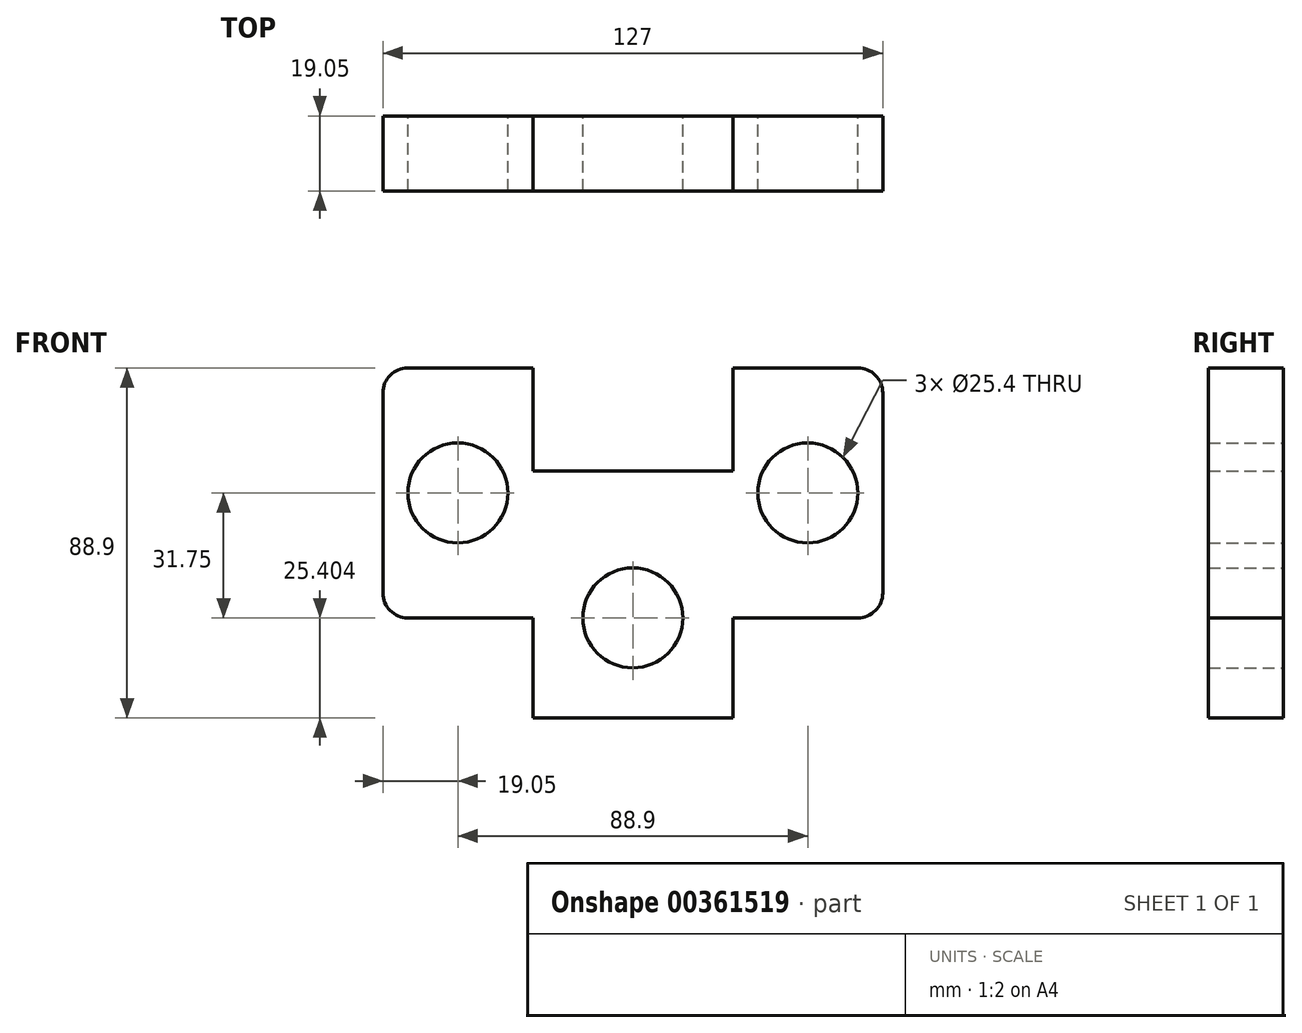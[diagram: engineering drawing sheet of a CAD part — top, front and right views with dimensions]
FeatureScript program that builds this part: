
annotation { "Feature Type Name" : "Feature", "Feature Type Description" : "" }
export const myFeature = defineFeature(function(context is Context, id is Id, definition is map)
    precondition{}
    {
        {
            var Q0;
            Q0=qCreatedBy(makeId("Front.planeOp"),FACE);
            var sketch = newSketch(context, id + "F0", { "sketchPlane" : qUnion([Q0])});
            skLineSegment(sketch, "E0", {"start": v(-74.8, 46.27) * mm, "end": v(-43.06, 46.27) * mm});
            skLineSegment(sketch, "E1", {"start": v(-43.06, 46.27) * mm, "end": v(-43.06, 20.11) * mm});
            skLineSegment(sketch, "E2", {"start": v(-43.06, 20.11) * mm, "end": v(7.74, 20.11) * mm});
            skLineSegment(sketch, "E3", {"start": v(7.74, 20.11) * mm, "end": v(7.74, 46.27) * mm});
            skLineSegment(sketch, "E4", {"start": v(7.74, 46.27) * mm, "end": v(39.5, 46.27) * mm});
            skLineSegment(sketch, "E5", {"start": v(45.84, 39.92) * mm, "end": v(45.84, -10.88) * mm});
            skLineSegment(sketch, "E6", {"start": v(39.5, -17.23) * mm, "end": v(7.74, -17.23) * mm});
            skLineSegment(sketch, "E7", {"start": v(7.74, -17.23) * mm, "end": v(7.74, -42.63) * mm});
            skLineSegment(sketch, "E8", {"start": v(-81.16, 39.92) * mm, "end": v(-81.16, -10.88) * mm});
            skLineSegment(sketch, "E9", {"start": v(-74.8, -17.23) * mm, "end": v(-43.06, -17.23) * mm});
            skLineSegment(sketch, "E10", {"start": v(-43.06, -17.23) * mm, "end": v(-43.06, -42.63) * mm});
            skLineSegment(sketch, "E11", {"start": v(-43.06, -42.63) * mm, "end": v(7.74, -42.63) * mm});
            skCircle(sketch, "E12", {"center": v(-62.1, 14.52) * mm, "radius": 12.7 * mm});
            skCircle(sketch, "E13", {"center": v(26.8, 14.52) * mm, "radius": 12.7 * mm});
            skCircle(sketch, "E14", {"center": v(-17.66, -17.23) * mm, "radius": 12.7 * mm});
            skPoint(sketch, "E15.visualSharp", {"position": v(-81.16, 46.27) * mm});
            skArc(sketch, "E15.filletArc", {"start": v(-74.8, 46.27) * mm, "mid": v(-79.3, 44.41) * mm, "end": v(-81.16, 39.92) * mm});
            skPoint(sketch, "E16.visualSharp", {"position": v(45.84, 46.27) * mm});
            skArc(sketch, "E16.filletArc", {"start": v(45.84, 39.92) * mm, "mid": v(43.98, 44.41) * mm, "end": v(39.5, 46.27) * mm});
            skPoint(sketch, "E17.visualSharp", {"position": v(45.84, -17.23) * mm});
            skArc(sketch, "E17.filletArc", {"start": v(39.5, -17.23) * mm, "mid": v(43.98, -15.37) * mm, "end": v(45.84, -10.88) * mm});
            skPoint(sketch, "E18.visualSharp", {"position": v(-81.16, -17.23) * mm});
            skArc(sketch, "E18.filletArc", {"start": v(-81.16, -10.88) * mm, "mid": v(-79.3, -15.37) * mm, "end": v(-74.8, -17.23) * mm});
            skSolve(sketch);
        }
        {
            var Q0;
            Q0 = qSketchRegion(id + "F0", true);
            extrude(context, id + "F1", {"entities" : qUnion([Q0]), "depth" : 19.05 * mm});
        }
    });
